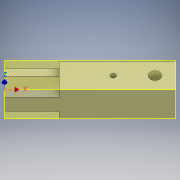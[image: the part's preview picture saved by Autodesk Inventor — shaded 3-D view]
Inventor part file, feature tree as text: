
AUTODESK INVENTOR PART (.ipt)
format: ipt  version: 2018 (Build 220112000, 112)  size: 403,968 bytes
history: native  units: in
note: dims shown in document units (in); Inventor stores cm internally (conversion verified against a paired STEP export)
features: extrude x5, sketch x5
ambient origin geometry x8: Origin, YZ Plane, XZ Plane, XY Plane, X Axis, Y Axis, Z Axis, Center Point
bodies: Solid1 (feature_tree)
feature tree (10):
  extrude  "Extrusion1"  Depth=0.74in
  extrude  "Extrusion2"  Depth=0.25in
  extrude  "Extrusion3"  Depth=0.375in
  extrude  "Extrusion4"  Depth=0.74in
  extrude  "Extrusion5"  Depth=2.125in
  sketch  "Sketch1"  dims[d0=0.74in d1=3.125in]
  sketch  "Sketch2"  dims[d2=0.74in d3=0.0in d4=0.25in]
  sketch  "Sketch3"  dims[d5=0.37in d6=0.375in]
  sketch  "Sketch4"  dims[d7=0.74in d8=0.0in d9=0.125in]
  sketch  "Sketch5"  dims[d10=0.37in d11=1.137in d12=0.37in d13=0.0in d14=0.5in d15=0.37in d16=0.37in d17=2.125in d18=0.0in d19=2.125in d20=0.187in d21=0.187in d22=0.0in d23=2.125in d24=0.0in]
